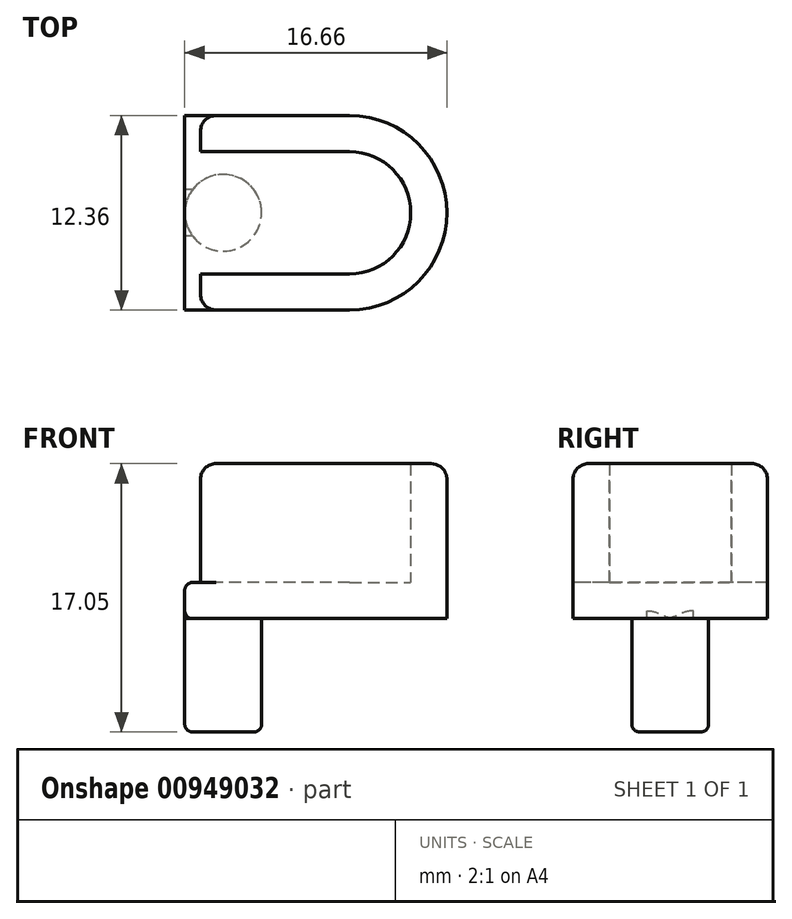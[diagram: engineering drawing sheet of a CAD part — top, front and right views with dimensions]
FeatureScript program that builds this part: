
annotation { "Feature Type Name" : "Feature", "Feature Type Description" : "" }
export const myFeature = defineFeature(function(context is Context, id is Id, definition is map)
    precondition{}
    {
        {
            var Q0;
            Q0=qCreatedBy(makeId("Top.planeOp"),FACE);
            var sketch = newSketch(context, id + "F0", { "sketchPlane" : qUnion([Q0])});
            skCircle(sketch, "E0", {"center": v(0, 0) * mm, "radius": 6.17 * mm});
            skLineSegment(sketch, "E1", {"start": v(6.17, 0) * mm, "end": v(-9.48, 0) * mm, "construction": true});
            skLineSegment(sketch, "E2", {"start": v(0, -6.17) * mm, "end": v(-9.48, -6.17) * mm});
            skLineSegment(sketch, "E3", {"start": v(0, 6.17) * mm, "end": v(-9.48, 6.17) * mm});
            skLineSegment(sketch, "E4", {"start": v(-9.48, 6.17) * mm, "end": v(-9.48, -6.17) * mm});
            skSolve(sketch);
        }
        {
            var Q0;
            {var subQ0=sQuery(id+"F0.wireOp",EDGE,"E0");var subQ1=makeQuery(id+"F0.imprint","INTERSECT",VERTEX,{"derivedFrom":[subQ0,sQuery(id+"F0.wireOp",EDGE,"E2")]});Q0=makeQuery(id+"F0.imprint","IMPRINT",FACE,{"disambiguationData":[TD([[makeQuery(id+"F0.imprint","IMPRINT",EDGE,{"disambiguationData":[TD([[subQ1,1.0]])],"derivedFrom":subQ0}),1.0]])]});}
            var Q1;
            {var subQ0=sQuery(id+"F0.wireOp",EDGE,"E2");Q1=makeQuery(id+"F0.imprint","IMPRINT",FACE,{"disambiguationData":[TD([[makeQuery(id+"F0.imprint","IMPRINT",EDGE,{"derivedFrom":subQ0}),-1.0]])]});}
            extrude(context, id + "F1", {"entities" : qUnion([Q0, Q1]), "depth" : 9.85 * mm, "offsetDistance" : 25 * mm});
        }
        {
            var Q0;
            Q0=makeQuery(id+"F1.opExtrude","CAP_FACE",FACE,{"disambiguationData":[OSD([sQuery(id+"F0.wireOp",EDGE,"E0"),sQuery(id+"F0.wireOp",EDGE,"E2"),sQuery(id+"F0.wireOp",EDGE,"E3"),sQuery(id+"F0.wireOp",EDGE,"E4")])],"isStart":false});
            shell(context, id + "F2", {"entities" : qUnion([Q0]), "thickness" : 2.3 * mm});
        }
        {
            var Q0;
            Q0=makeQuery(id+"F1.opExtrude","CAP_FACE",FACE,{"disambiguationData":[OSD([sQuery(id+"F0.wireOp",EDGE,"E0"),sQuery(id+"F0.wireOp",EDGE,"E2"),sQuery(id+"F0.wireOp",EDGE,"E3"),sQuery(id+"F0.wireOp",EDGE,"E4")])],"isStart":false});
            var sketch = newSketch(context, id + "F3", { "sketchPlane" : qUnion([Q0])});
            skLineSegment(sketch, "E5", {"start": v(-7.18, 3.88) * mm, "end": v(-9.48, 3.88) * mm});
            skLineSegment(sketch, "E6", {"start": v(-7.18, -3.88) * mm, "end": v(-9.48, -3.88) * mm});
            skSolve(sketch);
        }
        {
            var Q0;
            Q0 = qSketchRegion(id + "F3", true);
            var Q1;
            {var subQ0=sQuery(id+"F3.wireOp",EDGE,"E5");Q1=makeQuery(id+"F3.imprint","IMPRINT",FACE,{"disambiguationData":[TD([[makeQuery(id+"F3.imprint","IMPRINT",EDGE,{"derivedFrom":subQ0}),1.0]])]});}
            extrude(context, id + "F4", {"entities" : qUnion([Q0, Q1]), "operationType" : NewBodyOperationType.REMOVE, "oppositeDirection" : true, "depth" : 7.55 * mm, "offsetDistance" : 25 * mm});
        }
        {
            var Q0;
            Q0=makeQuery(id+"F1.opExtrude","SWEPT_FACE",FACE,{"disambiguationData":[OSD([sQuery(id+"F0.wireOp",EDGE,"E4")])]});
            var sketch = newSketch(context, id + "F5", { "sketchPlane" : qUnion([Q0])});
            skLineSegment(sketch, "E7", {"start": v(-3.88, 2.3) * mm, "end": v(-6.17, 2.3) * mm});
            skLineSegment(sketch, "E8", {"start": v(3.88, 2.3) * mm, "end": v(6.17, 2.3) * mm});
            skSolve(sketch);
        }
        {
            var Q0;
            {var subQ4=sQuery(id+"F5.wireOp",EDGE,"E7");Q0=makeQuery(id+"F5.imprint","IMPRINT",FACE,{"disambiguationData":[TD([[makeQuery(id+"F5.imprint","IMPRINT",EDGE,{"derivedFrom":subQ4}),1.0]])]});}
            extrude(context, id + "F6", {"entities" : qUnion([Q0]), "operationType" : NewBodyOperationType.ADD, "depth" : 1 * mm, "offsetDistance" : 25 * mm});
        }
        {
            var Q0;
            {var subQ0=sQuery(id+"F0.wireOp",EDGE,"E4");Q0=makeQuery(id+"F6.boolean.opBoolean","MERGE",FACE,{"derivedFrom":[makeQuery(id+"F1.opExtrude","CAP_FACE",FACE,{"disambiguationData":[OSD([sQuery(id+"F0.wireOp",EDGE,"E0"),sQuery(id+"F0.wireOp",EDGE,"E2"),sQuery(id+"F0.wireOp",EDGE,"E3"),subQ0])],"isStart":true}),makeQuery(id+"F6.opExtrude","SWEPT_FACE",FACE,{"disambiguationData":[OSD([subQ0])]})]});}
            var sketch = newSketch(context, id + "F7", { "sketchPlane" : qUnion([Q0])});
            skLineSegment(sketch, "E9", {"start": v(0, 0) * mm, "end": v(-10.48, 0) * mm, "construction": true});
            skLineSegment(sketch, "E10", {"start": v(-10.48, 0) * mm, "end": v(-8.04, 0) * mm, "construction": true});
            skCircle(sketch, "E11", {"center": v(-8.04, 0) * mm, "radius": 2.44 * mm});
            skSolve(sketch);
        }
        {
            var Q0;
            Q0=makeQuery(id+"F7.imprint","IMPRINT",FACE,{"disambiguationData":[TD([[makeQuery(id+"F7.imprint","IMPRINT",EDGE,{"derivedFrom":sQuery(id+"F7.wireOp",EDGE,"E11")}),1.0]])]});
            extrude(context, id + "F8", {"entities" : qUnion([Q0]), "operationType" : NewBodyOperationType.ADD, "depth" : 7.2 * mm, "offsetDistance" : 25 * mm});
        }
        {
            var Q0;
            Q0=makeQuery(id+"F8.opExtrude","CAP_EDGE",EDGE,{"disambiguationData":[OSD([sQuery(id+"F7.wireOp",EDGE,"E11")])],"isStart":false});
            fillet(context, id + "F9", {"entities" : qUnion([Q0]), "radius" : 0.5 * mm, "tangentPropagation" : true, "allowEdgeOverflow" : false});
        }
        {
            var Q0;
            Q0=makeQuery(id+"F4.boolean.opBoolean","COPY",EDGE,{"derivedFrom":makeQuery(id+"F4.opExtrude","SWEPT_EDGE",EDGE,{"disambiguationData":[OSD([sQuery(id+"F0.wireOp",EDGE,"E4"),sQuery(id+"F3.wireOp",EDGE,"E5")])]})});
            var Q1;
            Q1=makeQuery(id+"F1.opExtrude","SWEPT_EDGE",EDGE,{"disambiguationData":[OSD([sQuery(id+"F0.wireOp",EDGE,"E3"),sQuery(id+"F0.wireOp",EDGE,"E4")])]});
            var Q2;
            Q2=makeQuery(id+"F1.opExtrude","SWEPT_EDGE",EDGE,{"disambiguationData":[OSD([sQuery(id+"F0.wireOp",EDGE,"E2"),sQuery(id+"F0.wireOp",EDGE,"E4")])]});
            var Q3;
            Q3=makeQuery(id+"F4.boolean.opBoolean","COPY",EDGE,{"derivedFrom":makeQuery(id+"F4.opExtrude","SWEPT_EDGE",EDGE,{"disambiguationData":[OSD([sQuery(id+"F0.wireOp",EDGE,"E4"),sQuery(id+"F3.wireOp",EDGE,"E6")])]})});
            var Q4;
            Q4=makeQuery(id+"F1.opExtrude","CAP_EDGE",EDGE,{"disambiguationData":[OSD([sQuery(id+"F0.wireOp",EDGE,"E2")])],"isStart":false});
            var Q5;
            {var subQ0=sQuery(id+"F0.wireOp",EDGE,"E2");Q5=makeQuery(id+"F4.boolean.opBoolean","MERGE",EDGE,{"derivedFrom":[makeQuery(id+"F2.opShell","OFFSET_EDGE",EDGE,{"disambiguationData":[OSD([subQ0]),TDD([makeQuery(id+"F1.opExtrude","CAP_EDGE",EDGE,{"disambiguationData":[OSD([subQ0])],"isStart":false})])]})],"fromTools":[makeQuery(id+"F4.opExtrude","CAP_EDGE",EDGE,{"disambiguationData":[OSD([sQuery(id+"F3.wireOp",EDGE,"E6")])],"isStart":true})]});}
            var Q6;
            {var subQ0=sQuery(id+"F0.wireOp",EDGE,"E4");var subQ1=sQuery(id+"F0.wireOp",EDGE,"E3");Q6=makeQuery(id+"F4.boolean.opBoolean","SPLIT",EDGE,{"disambiguationData":[TD([makeQuery(id+"F1.opExtrude","SWEPT_FACE",FACE,{"disambiguationData":[OSD([subQ1])]})])],"derivedFrom":makeQuery(id+"F1.opExtrude","CAP_EDGE",EDGE,{"disambiguationData":[OSD([subQ0])],"isStart":false})});}
            var Q7;
            {var subQ0=sQuery(id+"F0.wireOp",EDGE,"E4");var subQ1=sQuery(id+"F0.wireOp",EDGE,"E2");Q7=makeQuery(id+"F4.boolean.opBoolean","SPLIT",EDGE,{"disambiguationData":[TD([makeQuery(id+"F1.opExtrude","SWEPT_FACE",FACE,{"disambiguationData":[OSD([subQ1])]})])],"derivedFrom":makeQuery(id+"F1.opExtrude","CAP_EDGE",EDGE,{"disambiguationData":[OSD([subQ0])],"isStart":false})});}
            fillet(context, id + "F10", {"entities" : qUnion([Q0, Q1, Q2, Q3, Q4, Q5, Q6, Q7]), "radius" : 1 * mm, "tangentPropagation" : true, "allowEdgeOverflow" : false});
        }
        {
            var Q0;
            Q0=makeQuery(id+"F6.opExtrude","CAP_EDGE",EDGE,{"disambiguationData":[OSD([sQuery(id+"F0.wireOp",EDGE,"E4"),sQuery(id+"F5.wireOp",EDGE,"E7"),sQuery(id+"F5.wireOp",EDGE,"E8")])],"isStart":false});
            var Q1;
            {var subQ0=sQuery(id+"F0.wireOp",EDGE,"E4");var subQ2=sQuery(id+"F0.wireOp",EDGE,"E2");Q1=makeQuery(id+"F8.boolean.opBoolean","SPLIT",EDGE,{"disambiguationData":[TD([makeQuery(id+"F1.opExtrude","SWEPT_FACE",FACE,{"disambiguationData":[OSD([subQ2])]})])],"derivedFrom":makeQuery(id+"F6.opExtrude","CAP_EDGE",EDGE,{"disambiguationData":[OSD([subQ0])],"isStart":false})});}
            fillet(context, id + "F11", {"entities" : qUnion([Q0, Q1]), "radius" : .5 * mm, "tangentPropagation" : true, "allowEdgeOverflow" : false});
        }
    });
